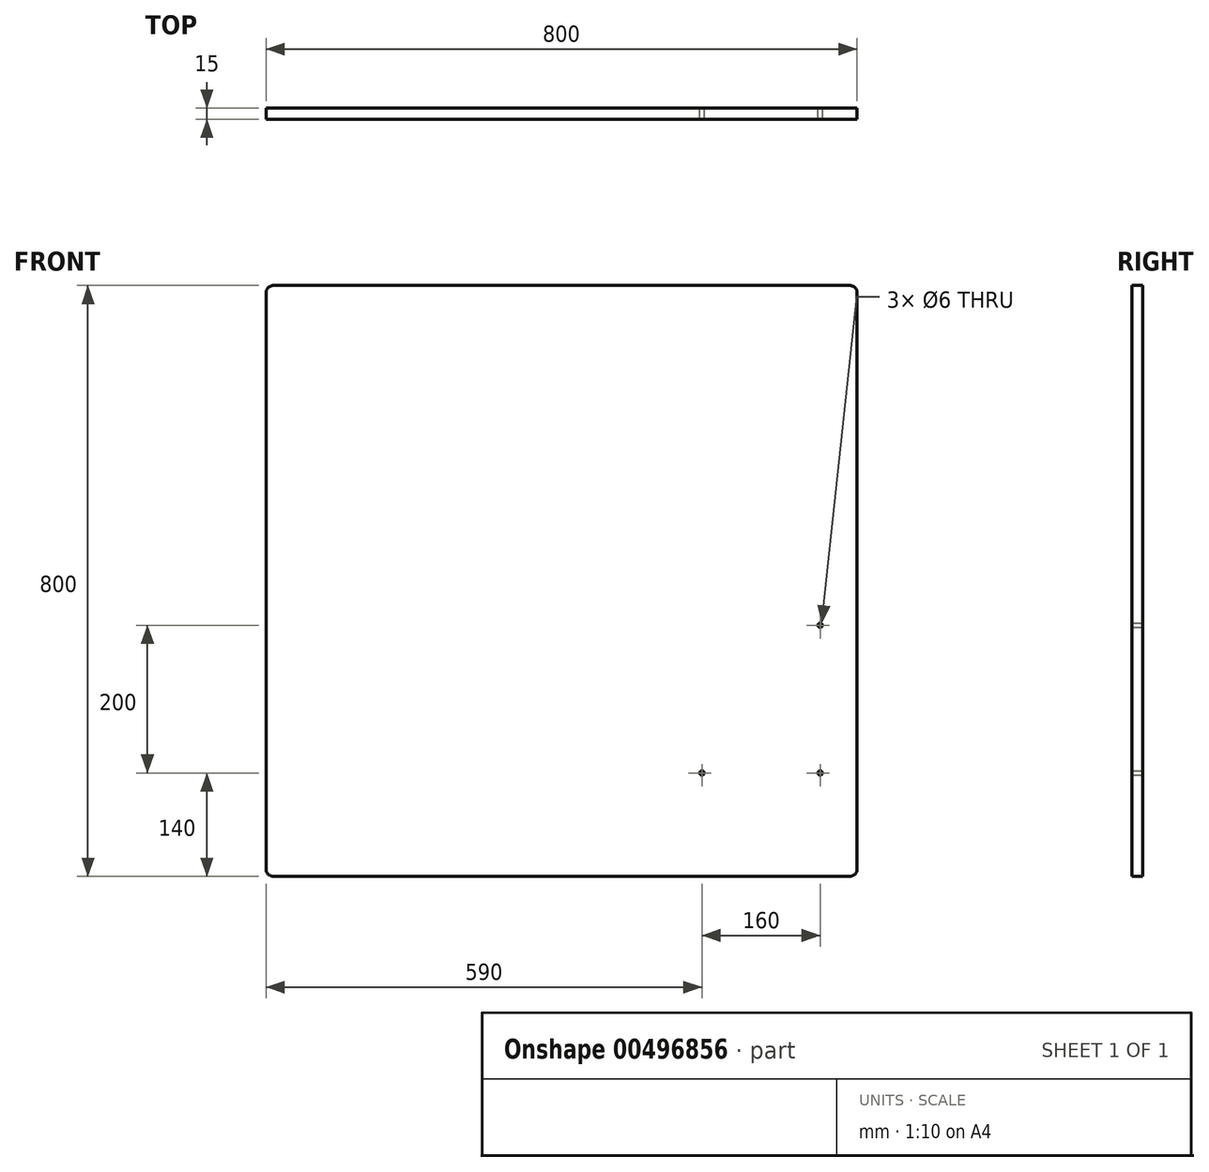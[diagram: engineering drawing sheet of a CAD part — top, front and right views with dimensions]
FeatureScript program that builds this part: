
annotation { "Feature Type Name" : "Feature", "Feature Type Description" : "" }
export const myFeature = defineFeature(function(context is Context, id is Id, definition is map)
    precondition{}
    {
        {
            var Q0;
            Q0=qCreatedBy(makeId("Front.planeOp"),FACE);
            var sketch = newSketch(context, id + "F0", { "sketchPlane" : qUnion([Q0])});
            skLineSegment(sketch, "E0.bottom", {"start": v(390, 400) * mm, "end": v(-390, 400) * mm});
            skLineSegment(sketch, "E0.top", {"start": v(390, -400) * mm, "end": v(-390, -400) * mm});
            skLineSegment(sketch, "E0.left", {"start": v(400, 390) * mm, "end": v(400, -390) * mm});
            skLineSegment(sketch, "E0.right", {"start": v(-400, 390) * mm, "end": v(-400, -390) * mm});
            skPoint(sketch, "E0.middle", {"position": v(0, 0) * mm});
            skCircle(sketch, "E1", {"center": v(190, -260) * mm, "radius": 3 * mm});
            skCircle(sketch, "E2", {"center": v(350, -60) * mm, "radius": 3 * mm});
            skCircle(sketch, "E3", {"center": v(350, -260) * mm, "radius": 3 * mm});
            skCircle(sketch, "E4", {"center": v(190, -460) * mm, "radius": 3 * mm});
            skPoint(sketch, "E5.visualSharp", {"position": v(-400, 400) * mm});
            skArc(sketch, "E5.filletArc", {"start": v(-390, 400) * mm, "mid": v(-397.07, 397.07) * mm, "end": v(-400, 390) * mm});
            skPoint(sketch, "E6.visualSharp", {"position": v(400, 400) * mm});
            skArc(sketch, "E6.filletArc", {"start": v(400, 390) * mm, "mid": v(397.07, 397.07) * mm, "end": v(390, 400) * mm});
            skPoint(sketch, "E7.visualSharp", {"position": v(-400, -400) * mm});
            skArc(sketch, "E7.filletArc", {"start": v(-400, -390) * mm, "mid": v(-397.07, -397.07) * mm, "end": v(-390, -400) * mm});
            skPoint(sketch, "E8.visualSharp", {"position": v(400, -400) * mm});
            skArc(sketch, "E8.filletArc", {"start": v(390, -400) * mm, "mid": v(397.07, -397.07) * mm, "end": v(400, -390) * mm});
            skSolve(sketch);
        }
        {
            var Q0;
            Q0=makeQuery(id+"F0.imprint","IMPRINT",FACE,{"disambiguationData":[TD([[makeQuery(id+"F0.imprint","IMPRINT",EDGE,{"derivedFrom":sQuery(id+"F0.wireOp",EDGE,"E0.bottom")}),1.0]])]});
            extrude(context, id + "F1", {"entities" : qUnion([Q0]), "depth" : 15 * mm, "offsetDistance" : 25 * mm});
        }
    });
